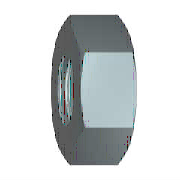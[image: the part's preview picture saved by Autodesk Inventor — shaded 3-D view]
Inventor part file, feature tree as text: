
AUTODESK INVENTOR PART (.ipt)
format: ipt  version: 2022.1 (Build 261234000, 234)  size: 164,352 bytes
history: native  units: mm (DEFAULTED — no unit token found)
features: sketch x3, extrude x1, chamfer x1, hole x1, other x1, plane x1
ambient origin geometry x7: Origin, YZ Plane, XZ Plane, X Axis, Y Axis, Z Axis, Center Point
bodies: Solid1 (feature_tree)
feature tree (8):
  extrude  "Cuerpo"  Depth=3.2mm
  chamfer  "Chaflán1"  Angle=30.0deg  [1 undecoded]
  hole  "Rosca"  [1 undecoded]
  other  "Work Axis1"
  plane  "Work Plane1"
  sketch  "Boceto1"  dims[d0=8.082904mm d1=3.2mm]
  sketch  "Boceto2"  dims[d2=0.0mm]
  sketch  "Boceto3"  dims[d3=30.0deg d4=30.0deg d5=5.9mm d6=5.9mm d7=90.0deg d25=3.242mm d26=6.0mm d27=4.0mm d28=2.0mm d29=14.3117mm d30=8.0mm d31=20.594885mm d8=0.378886mm d9=30.0deg d10=0.378886mm d11=30.0deg d13=0.0mm d14=0.0mm d39=0.0mm d40=0.378886mm d41=0.378886mm d42=0.0mm]
note: 2 required parameter values undecoded (feature->parameter linkage not recoverable at this tier; creation-order binding heuristic only, values carry confidence <= 0.55)
